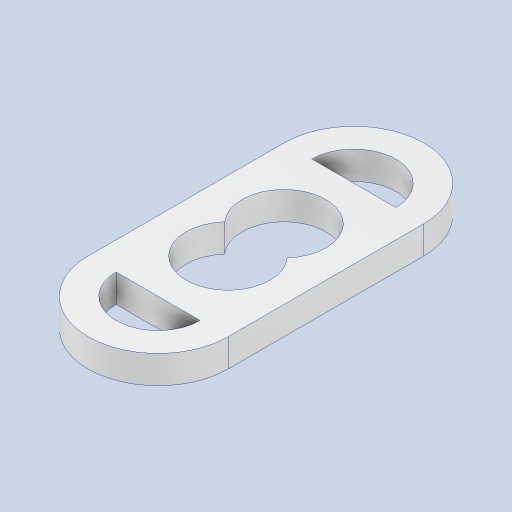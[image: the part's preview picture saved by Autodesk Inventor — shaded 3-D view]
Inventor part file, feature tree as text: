
AUTODESK INVENTOR PART (.ipt)
format: ipt  version: 2024 (Build 280153000, 153)  size: 169,984 bytes
history: native  units: mm
features: extrude x1, sketch x1
ambient origin geometry x8: Origin, YZ Plane, XZ Plane, XY Plane, X Axis, Y Axis, Z Axis, Center Point
bodies: Body1 (feature_tree)
feature tree (2):
  extrude  "Extrusión6"  Depth=10.0mm
  sketch  "Boceto1"  dims[d3=10.0mm d6=0.0mm d22=30.0mm d23=30.0mm d24=20.0mm d25=10.0mm d26=10.0mm d27=0.0mm d16=1.0mm d17=1.0mm d18=1.0mm d19=0.15mm d20=0.25mm d21=0.375mm]
